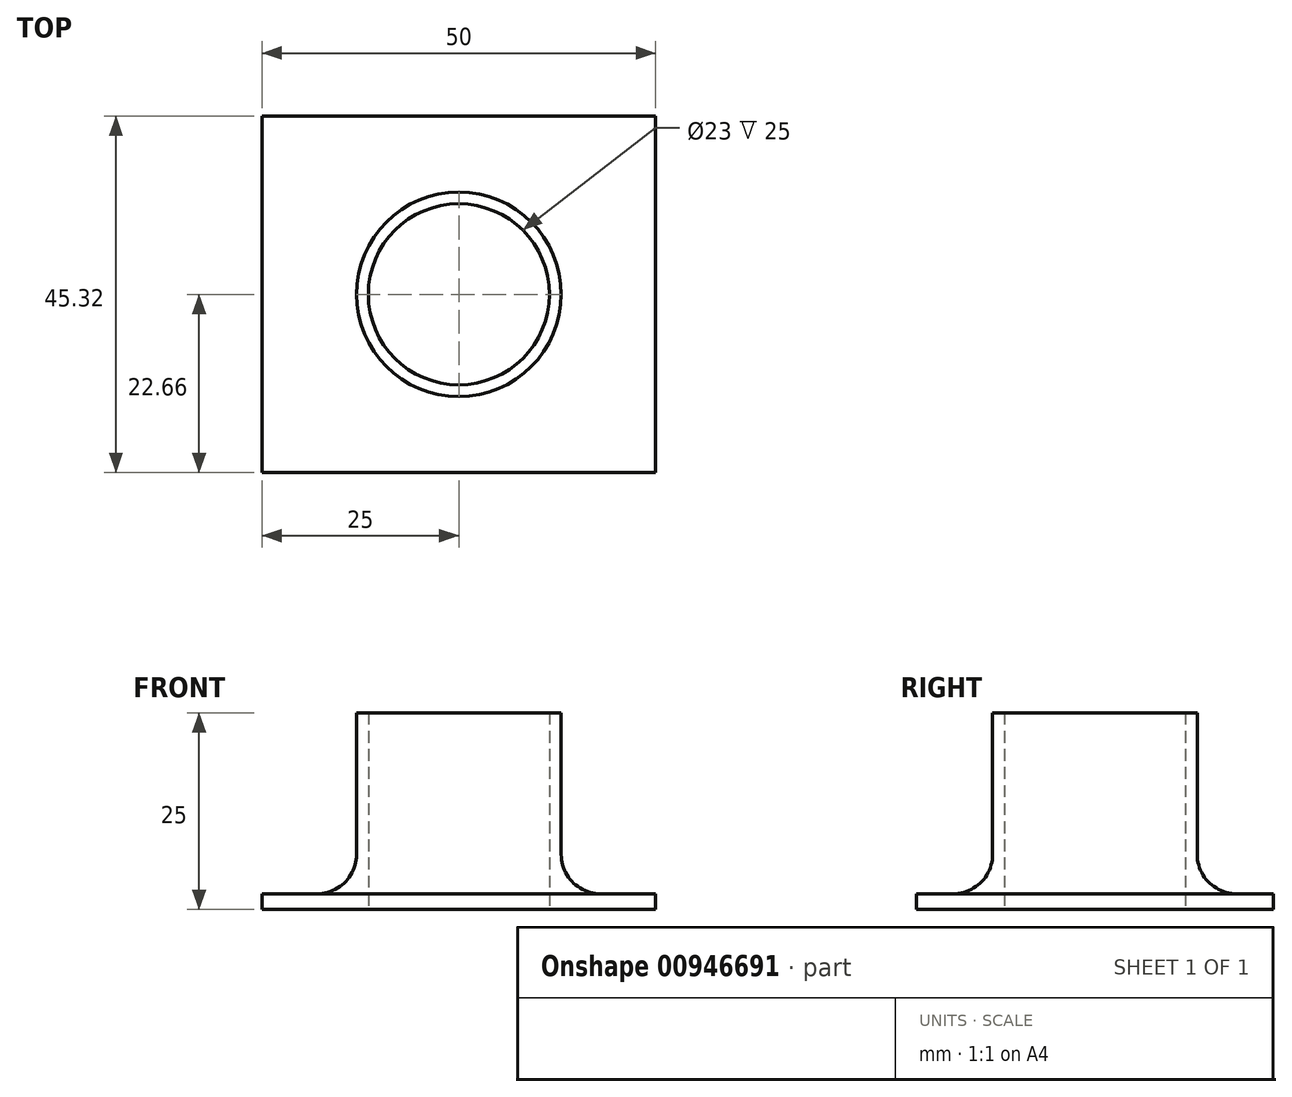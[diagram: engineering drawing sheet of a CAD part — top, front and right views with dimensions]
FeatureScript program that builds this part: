
annotation { "Feature Type Name" : "Feature", "Feature Type Description" : "" }
export const myFeature = defineFeature(function(context is Context, id is Id, definition is map)
    precondition{}
    {
        {
            var Q0;
            Q0=qCreatedBy(makeId("Top.planeOp"),FACE);
            var sketch = newSketch(context, id + "F0", { "sketchPlane" : qUnion([Q0])});
            skCircle(sketch, "E0", {"center": v(0, 0) * mm, "radius": 11.5 * mm});
            skCircle(sketch, "E1", {"center": v(0, 0) * mm, "radius": 13 * mm});
            skSolve(sketch);
        }
        {
            var Q0;
            Q0=qCreatedBy(makeId("Top.planeOp"),FACE);
            var sketch = newSketch(context, id + "F1", { "sketchPlane" : qUnion([Q0])});
            skLineSegment(sketch, "E2.bottom", {"start": v(-25, -22.66) * mm, "end": v(25, -22.66) * mm});
            skLineSegment(sketch, "E2.top", {"start": v(-25, 22.66) * mm, "end": v(25, 22.66) * mm});
            skLineSegment(sketch, "E2.left", {"start": v(-25, -22.66) * mm, "end": v(-25, 22.66) * mm});
            skLineSegment(sketch, "E2.right", {"start": v(25, -22.66) * mm, "end": v(25, 22.66) * mm});
            skPoint(sketch, "E2.middle", {"position": v(0, 0) * mm});
            skSolve(sketch);
        }
        {
            var Q0;
            Q0=makeQuery(id+"F1.imprint","IMPRINT",FACE,{"disambiguationData":[TD([[makeQuery(id+"F1.imprint","IMPRINT",EDGE,{"derivedFrom":sQuery(id+"F1.wireOp",EDGE,"E2.bottom")}),1.0]])]});
            extrude(context, id + "F2", {"entities" : qUnion([Q0]), "depth" : 2 * mm, "offsetDistance" : 25 * mm});
        }
        {
            var Q0;
            Q0 = qSketchRegion(id + "F0", true);
            extrude(context, id + "F3", {"entities" : qUnion([Q0]), "operationType" : NewBodyOperationType.ADD, "depth" : 25 * mm, "offsetDistance" : 25 * mm});
        }
        {
            var Q0;
            Q0=makeQuery(id+"F3.boolean.opBoolean","SPLIT",FACE,{"disambiguationData":[TD([makeQuery(id+"F3.opExtrude","SWEPT_FACE",FACE,{"disambiguationData":[OSD([sQuery(id+"F0.wireOp",EDGE,"E0")])]})])],"derivedFrom":makeQuery(id+"F2.opExtrude","CAP_FACE",FACE,{"disambiguationData":[OSD([sQuery(id+"F1.wireOp",EDGE,"E2.bottom"),sQuery(id+"F1.wireOp",EDGE,"E2.top"),sQuery(id+"F1.wireOp",EDGE,"E2.left"),sQuery(id+"F1.wireOp",EDGE,"E2.right")])],"isStart":false})});
            extrude(context, id + "F4", {"entities" : qUnion([Q0]), "operationType" : NewBodyOperationType.REMOVE, "oppositeDirection" : true, "depth" : 25 * mm, "offsetDistance" : 25 * mm});
        }
        {
            var Q0;
            Q0=makeQuery(id+"F3.boolean.opBoolean","INTERSECT",EDGE,{"derivedFrom":[makeQuery(id+"F2.opExtrude","CAP_FACE",FACE,{"disambiguationData":[OSD([sQuery(id+"F1.wireOp",EDGE,"E2.bottom"),sQuery(id+"F1.wireOp",EDGE,"E2.top"),sQuery(id+"F1.wireOp",EDGE,"E2.left"),sQuery(id+"F1.wireOp",EDGE,"E2.right")])],"isStart":false}),makeQuery(id+"F3.opExtrude","SWEPT_FACE",FACE,{"disambiguationData":[OSD([sQuery(id+"F0.wireOp",EDGE,"E1")])]})]});
            fillet(context, id + "F5", {"entities" : qUnion([Q0]), "radius" : 5 * mm, "tangentPropagation" : true, "allowEdgeOverflow" : false});
        }
    });
